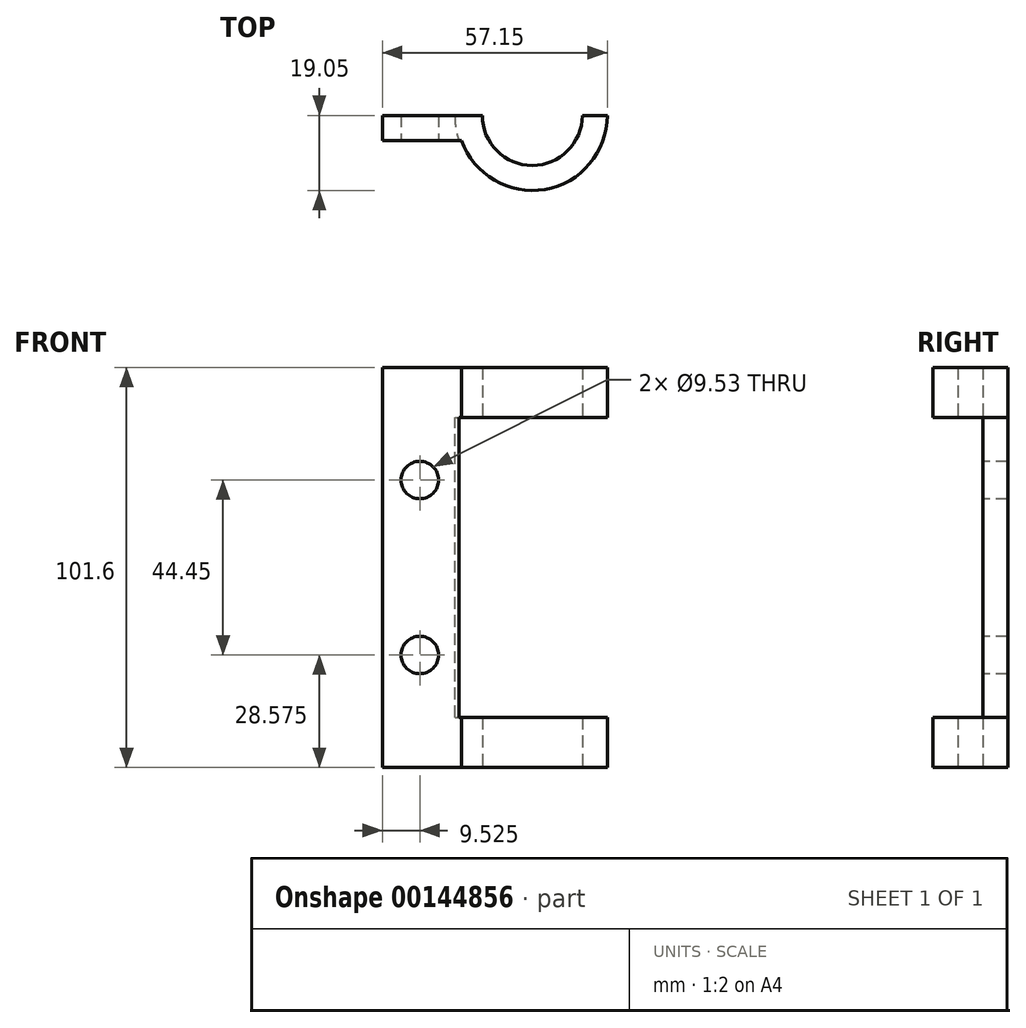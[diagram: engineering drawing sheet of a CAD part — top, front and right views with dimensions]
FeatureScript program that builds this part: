
annotation { "Feature Type Name" : "Feature", "Feature Type Description" : "" }
export const myFeature = defineFeature(function(context is Context, id is Id, definition is map)
    precondition{}
    {
        {
            var Q0;
            Q0=qCreatedBy(makeId("Top.planeOp"),FACE);
            var sketch = newSketch(context, id + "F0", { "sketchPlane" : qUnion([Q0])});
            skLineSegment(sketch, "E0", {"start": v(-38.1, 0) * mm, "end": v(-12.7, 0) * mm});
            skArc(sketch, "E1", {"start": v(-12.7, 0) * mm, "mid": v(0, -12.7) * mm, "end": v(12.7, 0) * mm});
            skArc(sketch, "E2", {"start": v(-17.96, -6.35) * mm, "mid": v(3.22, -18.78) * mm, "end": v(19.05, 0) * mm});
            skLineSegment(sketch, "E3", {"start": v(-38.1, 0) * mm, "end": v(-38.1, -6.35) * mm});
            skLineSegment(sketch, "E4", {"start": v(-38.1, -6.35) * mm, "end": v(-17.96, -6.35) * mm});
            skLineSegment(sketch, "E5", {"start": v(19.05, 0) * mm, "end": v(12.7, 0) * mm});
            skSolve(sketch);
        }
        {
            var Q0;
            Q0=makeQuery(id+"F0.imprint","IMPRINT",FACE,{"disambiguationData":[TD([[makeQuery(id+"F0.imprint","IMPRINT",EDGE,{"derivedFrom":sQuery(id+"F0.wireOp",EDGE,"E0")}),-1.0]])]});
            extrude(context, id + "F1", {"entities" : qUnion([Q0]), "endBound" : BoundingType.SYMMETRIC, "depth" : 101.6 * mm});
        }
        {
            var Q0;
            Q0=qCreatedBy(makeId("Top.planeOp"),FACE);
            var sketch = newSketch(context, id + "F2", { "sketchPlane" : qUnion([Q0])});
            skCircle(sketch, "E6", {"center": v(0, 0) * mm, "radius": 19.68 * mm});
            skSolve(sketch);
        }
        {
            var Q0;
            Q0=makeQuery(id+"F2.imprint","IMPRINT",FACE,{"disambiguationData":[TD([[makeQuery(id+"F2.imprint","IMPRINT",EDGE,{"derivedFrom":sQuery(id+"F2.wireOp",EDGE,"E6")}),1.0]])]});
            extrude(context, id + "F3", {"entities" : qUnion([Q0]), "operationType" : NewBodyOperationType.REMOVE, "endBound" : BoundingType.SYMMETRIC, "oppositeDirection" : true, "depth" : 76.2 * mm});
        }
        {
            var Q0;
            Q0=makeQuery(id+"F1.opExtrude","SWEPT_FACE",FACE,{"disambiguationData":[OSD([sQuery(id+"F0.wireOp",EDGE,"E4")])]});
            var sketch = newSketch(context, id + "F4", { "sketchPlane" : qUnion([Q0])});
            skCircle(sketch, "E7", {"center": v(-28.58, 22.22) * mm, "radius": 4.76 * mm});
            skCircle(sketch, "E8", {"center": v(-28.57, -22.23) * mm, "radius": 4.76 * mm});
            skLineSegment(sketch, "E9", {"start": v(-28.58, 22.22) * mm, "end": v(-28.58, -22.23) * mm, "construction": true});
            skSolve(sketch);
        }
        {
            var Q0;
            Q0 = qSketchRegion(id + "F4", true);
            extrude(context, id + "F5", {"entities" : qUnion([Q0]), "operationType" : NewBodyOperationType.REMOVE, "oppositeDirection" : true, "depth" : 12.7 * mm});
        }
    });
